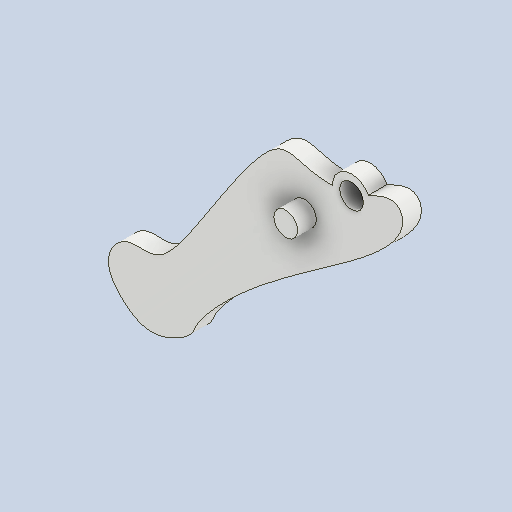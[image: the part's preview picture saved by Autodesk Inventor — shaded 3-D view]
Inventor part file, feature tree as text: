
AUTODESK INVENTOR PART (.ipt)
format: ipt  version: 2022 (Build 260153000, 153)  size: 134,144 bytes
history: native  units: in
note: dims shown in document units (in); Inventor stores cm internally (conversion verified against a paired STEP export)
features: extrude x2, sketch x1
ambient origin geometry x8: Origin, YZ Plane, XZ Plane, XY Plane, X Axis, Y Axis, Z Axis, Center Point
bodies: Solid1 (feature_tree)
feature tree (3):
  sketch  "Sketch2"  dims[d0=0.1969in d1=0.0in d2=0.1969in d3=0.0in]
  extrude  "Extrusion1"  Depth=0.1969in TaperAngle=0.0deg
  extrude  "Extrusion2"  [1 undecoded]
note: 1 required parameter value undecoded (feature->parameter linkage not recoverable at this tier; creation-order binding heuristic only, values carry confidence <= 0.55)
